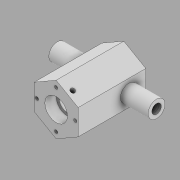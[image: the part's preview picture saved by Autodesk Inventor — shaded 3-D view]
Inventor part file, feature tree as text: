
AUTODESK INVENTOR PART (.ipt)
format: ipt  version: 2020 (Build 240168000, 168)  size: 170,496 bytes
history: native  units: in
note: dims shown in document units (in); Inventor stores cm internally (conversion verified against a paired STEP export)
features: sketch x7, hole x4, extrude x3, other x1, chamfer x1
ambient origin geometry x8: Origin, YZ Plane, XZ Plane, XY Plane, X Axis, Y Axis, Z Axis, Center Point
bodies: Body1 (feature_tree)
feature tree (16):
  other  "Sólido1"
  extrude  "Hexagono"  Depth=1.7in
  hole  "Tornillos"  [1 undecoded]
  extrude  "Extrusión2"  Depth=0.375in
  hole  "Agujero3"  [1 undecoded]
  chamfer  "Chaflán2"  Distance=1.125in
  extrude  "Extrusión3"  Depth=0.75in
  hole  "Agujero4"  [1 undecoded]
  hole  "Agujero5"  [1 undecoded]
  sketch  "Boceto1"  dims[d1=2.25in d2=1.7in]
  sketch  "Boceto2"  dims[d3=3.0in d4=0.0in d5=1.7in]
  sketch  "Boceto3"  dims[d6=0.145in d7=0.56in d8=0.375in d9=0.25in d10=0.5635in d11=0.56in d12=0.8108in d13=1.5in]
  sketch  "Boceto5"  dims[d14=1.5in d15=0.0in]
  sketch  "Boceto6"  dims[d26=0.75in d27=0.56in d28=1.0in d29=0.5in d30=0.5635in d31=0.63in d32=0.0in d33=0.375in d34=0.125in d35=45.0deg]
  sketch  "Boceto7"  dims[d36=0.75in]
  sketch  "Boceto8"  dims[d37=2.25in d38=1.125in d39=0.75in d40=4.4in d41=0.0in d42=0.417in d43=1.0in d44=0.5in d45=4.4in d46=0.5635in d47=1.385in d48=0.0in d49=0.25in d50=2.25in d51=1.125in d52=0.145in d53=0.38in d54=0.2in d55=0.375in d56=0.5635in d57=0.588in d58=0.0in]
note: 4 required parameter values undecoded (feature->parameter linkage not recoverable at this tier; creation-order binding heuristic only, values carry confidence <= 0.55)
